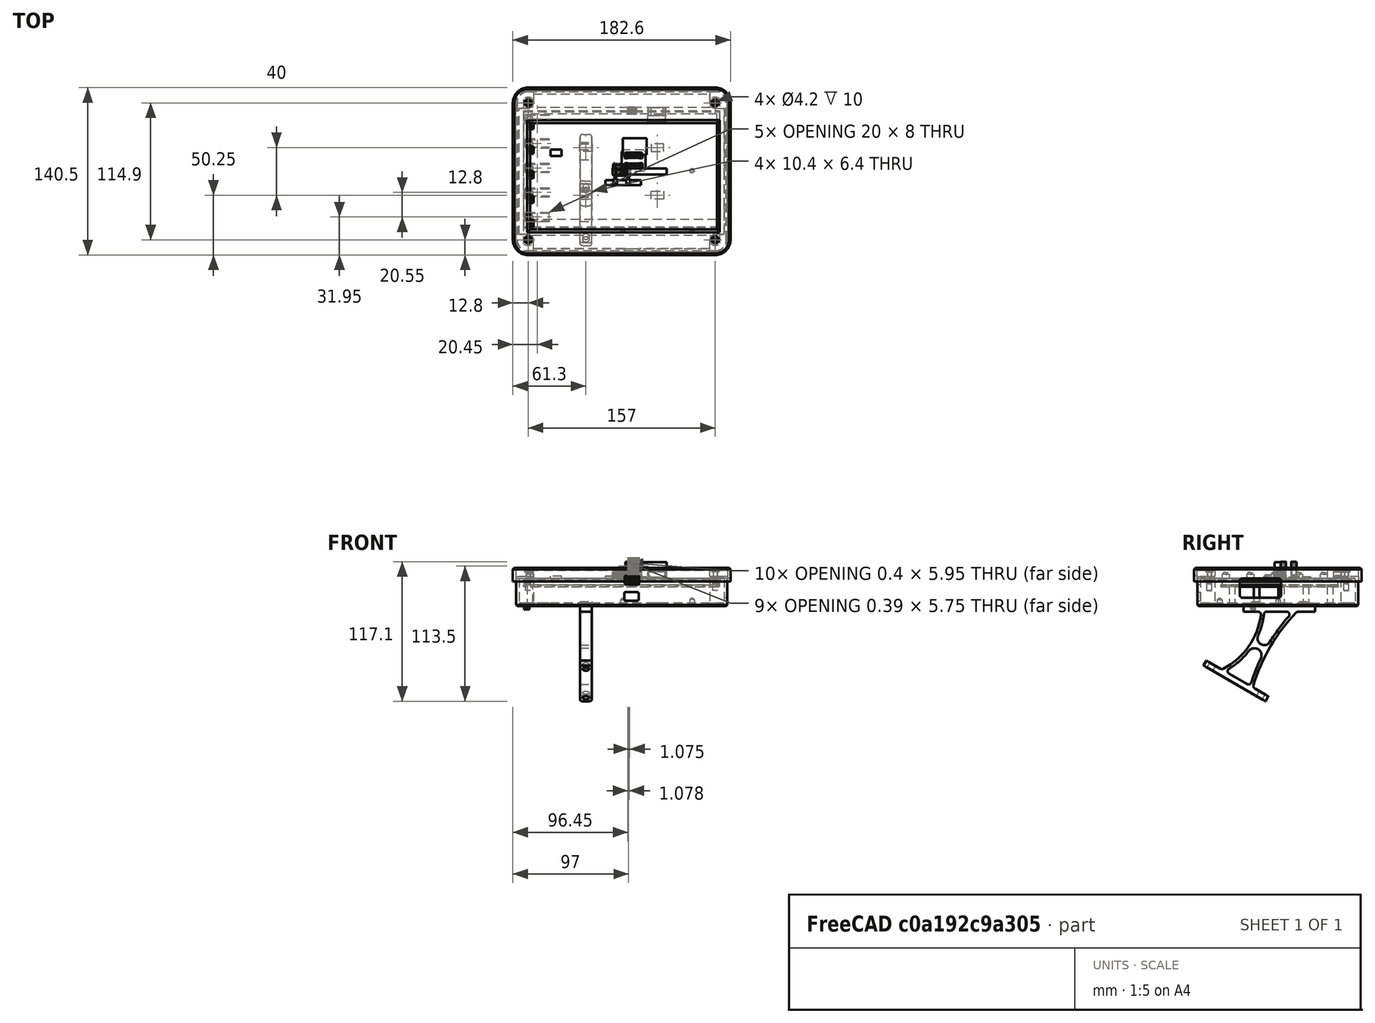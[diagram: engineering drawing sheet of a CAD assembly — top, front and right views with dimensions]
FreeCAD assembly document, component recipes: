
FREECAD ASSEMBLY — COMPONENT RECIPES ("rpi_screen")

This assembly document has 5 components, labeled P0..P4 below (a component is one placed body or linked part). 3 of them carry a construction recipe — the FreeCAD feature program that regenerates the part from scratch, quoted from this document or its linked companion documents; the rest are supplied as boundary geometry only. No exploded tour is included for this assembly.
COMPONENT P0 — geometry summary ("crystal_dfn4 v1"; no construction recipe available for this part):
  bounding box: 3.2 x 2.5 x 0.7 mm
  tessellated surface: 1,094 triangles
  volume: 3 mm^3 (62% of its bounding box)
  symmetry: 2-fold rotationally symmetric about the z axis; mirror-symmetric across its x mid-plane, y mid-plane
COMPONENT P1 — geometry summary ("Rpi+Screen"; no construction recipe available for this part):
  bounding box: 167.4 x 124.7 x 26.8 mm
  tessellated surface: 165,004 triangles
  volume: 114380 mm^3 (20% of its bounding box)
COMPONENT P2 — recipe-attached ("Ensemble boîtier inf", modeled in this document).
Construction recipe (the document's own serialized feature program — sketch geometry with constraints, then the solid features built on it; lengths are millimeters unless a unit is written):

FEATURE [PartDesign::SubShapeBinder] Binder
  BindMode = 0
  ClaimChildren = false
  Context = -> Part021 [Body.Binder.]
  Fuse = false
  MakeFace = true
  PartialLoad = false
  Relative = true
  Support = -> [Part020[Compound.Face122]]
  _Version = 2
FEATURE [Sketcher::SketchObject] Sketch
  ExternalGeometry = -> [Binder]
  FullyConstrained = true
  MapMode = 5
  Support = -> [XY_Plane]
  expr: Constraints[16] = <<Tableau>>.rayon_ext_boitier_inf
  sketch-geometry (8):
    g0: LineSegment StartX=-78.5 StartY=-67.45 StartZ=0 EndX=78.5 EndY=-67.45 EndZ=0
    g1: LineSegment StartX=88.5 StartY=-57.45 StartZ=0 EndX=88.5 EndY=57.45 EndZ=0
    g2: LineSegment StartX=78.5 StartY=67.45 StartZ=0 EndX=-78.5 EndY=67.45 EndZ=0
    g3: LineSegment StartX=-88.5 StartY=57.45 StartZ=0 EndX=-88.5 EndY=-57.45 EndZ=0
    g4: ArcOfCircle CenterX=78.5 CenterY=57.45 CenterZ=0 NormalX=0 NormalY=0 NormalZ=1 AngleXU=0 Radius=10 StartAngle=0 EndAngle=1.5708
    g5: ArcOfCircle CenterX=78.5 CenterY=-57.45 CenterZ=0 NormalX=0 NormalY=0 NormalZ=1 AngleXU=0 Radius=10 StartAngle=4.71239 EndAngle=6.28319
    g6: ArcOfCircle CenterX=-78.5 CenterY=-57.45 CenterZ=0 NormalX=0 NormalY=0 NormalZ=1 AngleXU=0 Radius=10 StartAngle=3.14159 EndAngle=4.71239
    g7: ArcOfCircle CenterX=-78.5 CenterY=57.45 CenterZ=0 NormalX=0 NormalY=0 NormalZ=1 AngleXU=0 Radius=10 StartAngle=1.5708 EndAngle=3.14159
  constraints (19):
    c: Horizontal(g0)
    c: Horizontal(g2)
    c: Vertical(g1)
    c: Vertical(g3)
    c: Tangent(g1,g4) = -1.5708
    c: Tangent(g2,g4) = -1.5708
    c: Tangent(g0,g5) = -1.5708
    c: Tangent(g1,g5) = -1.5708
    c: Tangent(g0,g6) = -1.5708
    c: Tangent(g3,g6) = -1.5708
    c: Tangent(g2,g7) = -1.5708
    c: Tangent(g3,g7) = -1.5708
    c: Equal(g7,g4)
    c: Coincident(g5,g-6)
    c: Coincident(g-3,g4)
    c: Coincident(g6,g-5)
    c: Radius(g4) = 10
    c: DistanceY(g0,g2) = 134.9
    c: DistanceX(g3,g1) = 177
FEATURE [PartDesign::Pad] Pad  label="Pad initial"
  Direction = (1,1,1)
  Length = 23
  Length2 = 100
  Profile = -> Sketch
  Refine = true
  Reversed = true
  Type = 0
FEATURE [Sketcher::SketchObject] Sketch001
  ExternalGeometry = -> [Binder,Sketch]
  FullyConstrained = true
  MapMode = 5
  Support = -> [XY_Plane]
  expr: Constraints[8] = <<Tableau>>.rayon
  expr: Constraints[1] = <<Tableau>>.B4
  sketch-geometry (20):
    g0: LineSegment StartX=-74 StartY=65.05 StartZ=0 EndX=74 EndY=65.05 EndZ=0
    g1: ArcOfCircle CenterX=78.5 CenterY=57.45 CenterZ=0 NormalX=0 NormalY=0 NormalZ=1 AngleXU=0 Radius=4.5 StartAngle=3.14159 EndAngle=4.71239
    g2: LineSegment StartX=86.1 StartY=52.95 StartZ=0 EndX=86.1 EndY=-52.95 EndZ=0
    g3: ArcOfCircle CenterX=78.5 CenterY=-57.45 CenterZ=0 NormalX=0 NormalY=0 NormalZ=1 AngleXU=0 Radius=4.5 StartAngle=1.5708 EndAngle=3.14159
    g4: LineSegment StartX=74 StartY=-65.05 StartZ=0 EndX=-74 EndY=-65.05 EndZ=0
    g5: ArcOfCircle CenterX=-78.5 CenterY=-57.45 CenterZ=0 NormalX=0 NormalY=0 NormalZ=1 AngleXU=0 Radius=4.5 StartAngle=6e-16 EndAngle=1.5708
    g6: LineSegment StartX=-86.1 StartY=-52.95 StartZ=0 EndX=-86.1 EndY=52.95 EndZ=0
    g7: ArcOfCircle CenterX=-78.5 CenterY=57.45 CenterZ=0 NormalX=0 NormalY=0 NormalZ=1 AngleXU=0 Radius=4.5 StartAngle=4.71239 EndAngle=6.28319
    g8: LineSegment StartX=74 StartY=65.05 StartZ=0 EndX=74 EndY=67.45 EndZ=0
    g9: LineSegment StartX=78.5 StartY=52.95 StartZ=0 EndX=86.1 EndY=52.95 EndZ=0
    g10: LineSegment StartX=74 StartY=57.45 StartZ=0 EndX=74 EndY=65.05 EndZ=0
    g11: LineSegment StartX=86.1 StartY=52.95 StartZ=0 EndX=88.5 EndY=52.95 EndZ=0
    g12: LineSegment StartX=86.1 StartY=-52.95 StartZ=0 EndX=78.5 EndY=-52.95 EndZ=0
    g13: LineSegment StartX=74 StartY=-65.05 StartZ=0 EndX=74 EndY=-57.45 EndZ=0
    g14: LineSegment StartX=74 StartY=-65.05 StartZ=0 EndX=74 EndY=-67.45 EndZ=0
    g15: LineSegment StartX=-74 StartY=-65.05 StartZ=0 EndX=-74 EndY=-57.45 EndZ=0
    g16: LineSegment StartX=-86.1 StartY=-52.95 StartZ=0 EndX=-78.5 EndY=-52.95 EndZ=0
    g17: LineSegment StartX=-86.1 StartY=52.95 StartZ=0 EndX=-78.5 EndY=52.95 EndZ=0
    g18: LineSegment StartX=-74 StartY=65.05 StartZ=0 EndX=-74 EndY=57.45 EndZ=0
    g19: LineSegment StartX=-88.5 StartY=52.95 StartZ=0 EndX=-86.1 EndY=52.95 EndZ=0
  constraints (52):
    c: Horizontal(g0)
    c: Distance(g0,g-7) = 2.4
    c: Coincident(g8,g0)
    c: PointOnObject(g8,g-7)
    c: Vertical(g8)
    c: Vertical(g6)
    c: Horizontal(g4)
    c: Vertical(g2)
    c: Radius(g1) = 4.5
    c: Equal(g7,g5)
    c: Equal(g5,g3)
    c: Equal(g3,g1)
    c: Coincident(g9,g2)
    c: Horizontal(g9)
    c: Coincident(g10,g0)
    c: Vertical(g10)
    c: Tangent(g1,g10) = 1.5708
    c: Tangent(g1,g9) = -1.5708
    c: Coincident(g1,g-6)
    c: Coincident(g11,g2)
    c: PointOnObject(g11,g-8)
    c: Horizontal(g11)
    c: Equal(g11,g8)
    c: Coincident(g12,g2)
    c: Horizontal(g12)
    c: Coincident(g13,g4)
    c: Vertical(g13)
    c: Tangent(g3,g13) = 1.5708
    c: Tangent(g3,g12) = -1.5708
    c: Coincident(g3,g-5)
    c: Coincident(g14,g4)
    c: PointOnObject(g14,g-10)
    c: Vertical(g14)
    c: Equal(g14,g11)
    c: Coincident(g15,g4)
    c: Vertical(g15)
    c: Coincident(g16,g6)
    c: Horizontal(g16)
    c: Tangent(g5,g16) = 1.5708
    c: Tangent(g5,g15) = -1.5708
    c: Coincident(g17,g6)
    c: Horizontal(g17)
    c: Tangent(g7,g17) = -1.5708
    c: Coincident(g18,g0)
    c: Vertical(g18)
    c: Tangent(g7,g18) = 1.5708
    c: Coincident(g19,g6)
    c: Horizontal(g19)
    c: PointOnObject(g19,g-9)
    c: Equal(g19,g8)
    c: Coincident(g7,g-3)
    c: Coincident(g5,g-4)
FEATURE [PartDesign::Pocket] Pocket  label="Evidement"
  BaseFeature = -> Pad
  Length = 0
  Length2 = 100
  Offset = -2.4
  Profile = -> Sketch001
  Refine = true
  Type = 3
  UpToFace = -> Pad [Face10]
  expr: Offset = -<<Tableau>>.B4
FEATURE [Sketcher::SketchObject] Sketch002
  ExternalGeometry = -> [Binder,Sketch001]
  FullyConstrained = false
  MapMode = 5
  Support = -> [XY_Plane]
  sketch-geometry (5):
    g0: Circle CenterX=78.5 CenterY=57.45 CenterZ=0 NormalX=0 NormalY=0 NormalZ=1 AngleXU=0 Radius=2.1
    g1: LineSegment StartX=76.6602 StartY=56.4374 StartZ=0 EndX=74.5577 EndY=55.2802 EndZ=0
    g2: Circle CenterX=78.5 CenterY=-57.45 CenterZ=0 NormalX=0 NormalY=0 NormalZ=1 AngleXU=0 Radius=2.1
    g3: Circle CenterX=-78.5 CenterY=-57.45 CenterZ=0 NormalX=0 NormalY=0 NormalZ=1 AngleXU=0 Radius=2.1
    g4: Circle CenterX=-78.5 CenterY=57.45 CenterZ=0 NormalX=0 NormalY=0 NormalZ=1 AngleXU=0 Radius=2.1
  constraints (13):
    c: Radius(g-3) = 1.6
    c: Coincident(g0,g-3)
    c: PointOnObject(g1,g0)
    c: PointOnObject(g1,g-7)
    c: Distance(g1) = 2.4
    c: PointOnObject(g0,g1)
    c: Coincident(g2,g-4)
    c: Coincident(g3,g-5)
    c: Coincident(g4,g-6)
    c: Equal(g4,g3)
    c: Equal(g3,g2)
    c: Equal(g2,g0)
    c: Radius(g0) = 2.1
FEATURE [PartDesign::Pocket] Pocket001  label="Insert"
  BaseFeature = -> Pocket
  Length = 10
  Length2 = 100
  Profile = -> Sketch002
  Refine = true
  Type = 0
FEATURE [PartDesign::SubShapeBinder] Binder001
  BindMode = 0
  ClaimChildren = false
  Context = -> Part021 [Body.Binder001.]
  Fuse = false
  MakeFace = true
  PartialLoad = false
  Relative = true
  Support = -> [Part020[Part018.Compound075.Face74]]
  _Version = 2
FEATURE [Sketcher::SketchObject] Sketch003
  AttachmentOffset = pos=(0,0,-20.6) rot=(0,0,1;0rad)
  ExternalGeometry = -> [Binder001]
  FullyConstrained = true
  MapMode = 5
  Placement = pos=(0,0,-20.6) rot=(0,0,1;0rad)
  Support = -> [XY_Plane]
  expr: .AttachmentOffset.Base.z = -Pad.Length + <<Tableau>>.B4
  sketch-geometry (4):
    g0: Circle CenterX=1.15 CenterY=-48.9 CenterZ=0 NormalX=0 NormalY=0 NormalZ=1 AngleXU=0 Radius=2
    g1: Circle CenterX=59.15 CenterY=-48.9 CenterZ=0 NormalX=0 NormalY=0 NormalZ=1 AngleXU=0 Radius=2
    g2: Circle CenterX=59.15 CenterY=0.1 CenterZ=0 NormalX=0 NormalY=0 NormalZ=1 AngleXU=0 Radius=2
    g3: Circle CenterX=1.15 CenterY=0.1 CenterZ=0 NormalX=0 NormalY=0 NormalZ=1 AngleXU=0 Radius=2
  constraints (8):
    c: Coincident(g0,g-4)
    c: Coincident(g1,g-5)
    c: Coincident(g2,g-6)
    c: Coincident(g3,g-3)
    c: Equal(g3,g2)
    c: Equal(g2,g1)
    c: Equal(g1,g0)
    c: Radius(g3) = 2
FEATURE [PartDesign::Pad] Pad001
  BaseFeature = -> Pocket001
  Direction = (1,1,1)
  Length = 10
  Length2 = 100
  Profile = -> Sketch003
  Refine = true
  Type = 3
  UpToFace = -> Binder001 [Face1]
FEATURE [Sketcher::SketchObject] Sketch004
  ExternalGeometry = -> [Binder001]
  FullyConstrained = true
  MapMode = 5
  Placement = pos=(0,-4.3e-15,-17.75) rot=(1,0,0;3.14159rad)
  Support = -> [Binder001]
  sketch-geometry (4):
    g0: Circle CenterX=1.15 CenterY=-0.1 CenterZ=0 NormalX=0 NormalY=0 NormalZ=1 AngleXU=0 Radius=1.2
    g1: Circle CenterX=59.15 CenterY=-0.1 CenterZ=0 NormalX=0 NormalY=0 NormalZ=1 AngleXU=0 Radius=1.2
    g2: Circle CenterX=59.15 CenterY=48.9 CenterZ=0 NormalX=0 NormalY=0 NormalZ=1 AngleXU=0 Radius=1.2
    g3: Circle CenterX=1.15 CenterY=48.9 CenterZ=0 NormalX=0 NormalY=0 NormalZ=1 AngleXU=0 Radius=1.2
  constraints (8):
    c: Coincident(g0,g-3)
    c: Coincident(g1,g-5)
    c: Coincident(g2,g-6)
    c: Coincident(g3,g-4)
    c: Equal(g3,g0)
    c: Equal(g0,g1)
    c: Equal(g1,g2)
    c: Radius(g0) = 1.2
FEATURE [PartDesign::Pad] Pad002
  BaseFeature = -> Pad001
  Direction = (1,1,1)
  Length = 1
  Length2 = 100
  Profile = -> Sketch004
  Refine = true
  Reversed = true
  Type = 0
FEATURE [PartDesign::Plane] DatumPlane
  AttachmentOffset = pos=(0,0,89) rot=(0,0,1;0rad)
  Length = 151.326
  MapMode = 5
  Placement = pos=(89,-1.98e-14,1.98e-14) rot=(0.57735,0.57735,0.57735;2.0944rad)
  ResizeMode = 0
  Support = -> [YZ_Plane]
  Width = 66.4256
FEATURE [PartDesign::SubShapeBinder] Binder008
  BindMode = 0
  ClaimChildren = false
  Context = -> Part021 [Body.Binder008.]
  Fuse = false
  MakeFace = true
  PartialLoad = false
  Relative = true
  Support = -> [Part020[Compound.Edge128,Compound.Edge136]]
  _Version = 2
FEATURE [PartDesign::SubShapeBinder] Binder009
  BindMode = 0
  ClaimChildren = false
  Context = -> Part021 [Body.Binder009.]
  Fuse = false
  MakeFace = true
  PartialLoad = false
  Relative = true
  Support = -> [Part020[Compound.Edge365,Compound.Edge925]]
  _Version = 2
FEATURE [PartDesign::SubShapeBinder] Binder010
  BindMode = 0
  ClaimChildren = false
  Context = -> Part021 [Body.Binder010.]
  Fuse = false
  MakeFace = true
  PartialLoad = false
  Relative = true
  Support = -> [Part020[Part018.Compound076.Edge439]]
  _Version = 2
FEATURE [Sketcher::SketchObject] Sketch006
  AttachmentOffset = pos=(0,0,69) rot=(0,0,1;0rad)
  ExternalGeometry = -> [Binder008,Binder009,Binder010]
  FullyConstrained = true
  MapMode = 5
  Placement = pos=(0,-69,-1.53e-14) rot=(1,0,0;1.5708rad)
  Support = -> [XZ_Plane]
  expr: Constraints[15] = <<Tableau>>.B2 * 30
  sketch-geometry (13):
    g0: LineSegment StartX=3.87439 StartY=2.425 StartZ=0 EndX=13.4744 EndY=2.425 EndZ=0
    g1: LineSegment StartX=14.6744 StartY=1.225 StartZ=0 EndX=14.6744 EndY=-3.875 EndZ=0
    g2: LineSegment StartX=13.4744 StartY=-5.075 StartZ=0 EndX=3.87439 EndY=-5.075 EndZ=0
    g3: LineSegment StartX=2.67439 StartY=-3.875 StartZ=0 EndX=2.67439 EndY=1.225 EndZ=0
    g4: ArcOfCircle CenterX=3.87439 CenterY=1.225 CenterZ=0 NormalX=0 NormalY=0 NormalZ=1 AngleXU=0 Radius=1.2 StartAngle=1.5708 EndAngle=3.14159
    g5: ArcOfCircle CenterX=13.4744 CenterY=1.225 CenterZ=0 NormalX=0 NormalY=0 NormalZ=1 AngleXU=0 Radius=1.2 StartAngle=0 EndAngle=1.5708
    g6: ArcOfCircle CenterX=13.4744 CenterY=-3.875 CenterZ=0 NormalX=0 NormalY=0 NormalZ=1 AngleXU=0 Radius=1.2 StartAngle=4.71239 EndAngle=6.28319
    g7: ArcOfCircle CenterX=3.87439 CenterY=-3.875 CenterZ=0 NormalX=0 NormalY=0 NormalZ=1 AngleXU=0 Radius=1.2 StartAngle=3.14159 EndAngle=4.71239
    g8: GeomPoint X=8.67439 Y=-1.369 Z=0
    g9: LineSegment StartX=8.67439 StartY=-1.369 StartZ=0 EndX=8.67439 EndY=-1.624 EndZ=0
    g10: LineSegment StartX=11.0744 StartY=-0.15 StartZ=0 EndX=11.0744 EndY=2.425 EndZ=0
    g11: LineSegment StartX=11.7744 StartY=-2.5 StartZ=0 EndX=11.7744 EndY=-5.075 EndZ=0
    g12: LineSegment StartX=8.24488 StartY=-16.15 StartZ=0 EndX=8.67439 EndY=-2.5 EndZ=0
  constraints (33):
    c: Horizontal(g0)
    c: Horizontal(g2)
    c: Vertical(g1)
    c: Vertical(g3)
    c: Tangent(g0,g4) = 1.5708
    c: Tangent(g3,g4) = 1.5708
    c: Tangent(g0,g5) = 1.5708
    c: Tangent(g1,g5) = 1.5708
    c: Tangent(g1,g6) = 1.5708
    c: Tangent(g2,g6) = 1.5708
    c: Tangent(g2,g7) = 1.5708
    c: Tangent(g3,g7) = 1.5708
    c: Equal(g4,g5)
    c: Equal(g5,g6)
    c: Equal(g6,g7)
    c: DistanceX(g3,g1) = 12
    c: Radius(g5) = 1.2
    c: DistanceY(g2,g0) = 7.5
    c: Symmetric(g-3,g-4,g8)
    c: Coincident(g9,g8)
    c: Equal(g9,g-4)
    c: Symmetric(g3,g1,g9)
    c: Coincident(g10,g-6)
    c: PointOnObject(g10,g0)
    c: Vertical(g10)
    c: Coincident(g11,g-5)
    c: PointOnObject(g11,g2)
    c: Vertical(g11)
    c: Equal(g11,g10)
    c: DistanceY(g-7,g-5) = 13.65
    c: Distance(g12) = 13.6568
    c: Symmetric(g-5,g-5,g12)
    c: Coincident(g12,g-7)
FEATURE [PartDesign::SubShapeBinder] Binder011
  BindMode = 0
  ClaimChildren = false
  Context = -> Part021 [Body.Binder011.]
  Fuse = false
  MakeFace = true
  PartialLoad = false
  Relative = true
  Support = -> [Part020[Part018.Compound079.Edge1280,Part018.Compound080.Edge1280,Part018.Compound079.Edge1555,Part018.Compound080.Edge1286]]
  _Version = 2
FEATURE [Sketcher::SketchObject] Sketch005
  ExternalGeometry = -> [Binder011]
  FullyConstrained = true
  MapMode = 5
  Placement = pos=(89,-1.98e-14,1.98e-14) rot=(0.57735,0.57735,0.57735;2.0944rad)
  Support = -> [DatumPlane]
  sketch-geometry (14):
    g0: LineSegment StartX=-29.5843 StartY=-16.175 StartZ=0 EndX=0.415691 EndY=-16.175 EndZ=0
    g1: LineSegment StartX=2.81569 StartY=-13.775 StartZ=0 EndX=2.81569 EndY=-2.175 EndZ=0
    g2: LineSegment StartX=0.415691 StartY=0.225 StartZ=0 EndX=-29.5843 EndY=0.225 EndZ=0
    g3: LineSegment StartX=-31.9843 StartY=-2.175 StartZ=0 EndX=-31.9843 EndY=-13.775 EndZ=0
    g4: ArcOfCircle CenterX=-29.5843 CenterY=-2.175 CenterZ=0 NormalX=0 NormalY=0 NormalZ=1 AngleXU=0 Radius=2.4 StartAngle=1.5708 EndAngle=3.14159
    g5: ArcOfCircle CenterX=0.415691 CenterY=-2.175 CenterZ=0 NormalX=0 NormalY=0 NormalZ=1 AngleXU=0 Radius=2.4 StartAngle=0 EndAngle=1.5708
    g6: ArcOfCircle CenterX=0.415691 CenterY=-13.775 CenterZ=0 NormalX=0 NormalY=0 NormalZ=1 AngleXU=0 Radius=2.4 StartAngle=4.71239 EndAngle=6.28319
    g7: ArcOfCircle CenterX=-29.5843 CenterY=-13.775 CenterZ=0 NormalX=0 NormalY=0 NormalZ=1 AngleXU=0 Radius=2.4 StartAngle=3.14159 EndAngle=4.71239
    g8: GeomPoint X=-14.5843 Y=-7.975 Z=0
    g9: LineSegment StartX=-23.7843 StartY=-0.5 StartZ=0 EndX=-31.9843 EndY=-0.5 EndZ=0
    g10: LineSegment StartX=-29.5843 StartY=0.225 StartZ=0 EndX=-31.9843 EndY=0.225 EndZ=0
    g11: LineSegment StartX=-31.9843 StartY=0.225 StartZ=0 EndX=-31.9843 EndY=-2.175 EndZ=0
    g12: LineSegment StartX=0.415691 StartY=0.225 StartZ=0 EndX=2.81569 EndY=0.225 EndZ=0
    g13: LineSegment StartX=2.81569 StartY=0.225 StartZ=0 EndX=2.81569 EndY=-2.175 EndZ=0
  constraints (34):
    c: Horizontal(g0)
    c: Horizontal(g2)
    c: Vertical(g1)
    c: Vertical(g3)
    c: Tangent(g2,g4) = -1.5708
    c: Tangent(g3,g4) = -1.5708
    c: Tangent(g1,g5) = -1.5708
    c: Tangent(g2,g5) = -1.5708
    c: Tangent(g0,g6) = -1.5708
    c: Tangent(g1,g6) = -1.5708
    c: Tangent(g0,g7) = -1.5708
    c: Tangent(g3,g7) = -1.5708
    c: Equal(g4,g5)
    c: Equal(g5,g6)
    c: Equal(g6,g7)
    c: DistanceX(g3,g1) = 34.8
    c: DistanceY(g0,g2) = 16.4
    c: Symmetric(g-3,g-4,g8)
    c: Symmetric(g7,g5,g8)
    c: Horizontal(g9)
    c: DistanceX(g9,g9) = 8.2
    c: PointOnObject(g9,g3)
    c: Symmetric(g-5,g-5,g9)
    c: Radius(g5) = 2.4
    c: Horizontal(g10)
    c: Coincident(g10,g11)
    c: Vertical(g11)
    c: Horizontal(g12)
    c: Coincident(g12,g13)
    c: Vertical(g13)
    c: Coincident(g10,g2)
    c: Coincident(g11,g3)
    c: Coincident(g2,g12)
    c: Coincident(g1,g13)
FEATURE [PartDesign::Pocket] Pocket002  label="USB"
  BaseFeature = -> Pad002
  Length = 3
  Length2 = 100
  Profile = -> Sketch005
  Refine = true
  Type = 0
  UpToFace = -> Pad002 [Face21]
FEATURE [PartDesign::Pocket] Pocket003  label="µUSB"
  BaseFeature = -> Pocket002
  Length = 5
  Length2 = 100
  Profile = -> Sketch006
  Refine = true
  Type = 0
FEATURE [PartDesign::LinearPattern] LinearPattern  label="Repetition µUSB"
  BaseFeature = -> Pocket003
  Direction = -> Sketch006 [Axis3]
  Length = 13.66
  Occurrences = 2
  Originals = -> [Pocket003]
  Refine = true
  Reversed = true
FEATURE [PartDesign::Chamfer] Chamfer
  Angle = 45
  Base = -> LinearPattern [Face5]
  BaseFeature = -> LinearPattern
  ChamferType = 0
  FlipDirection = false
  Refine = true
  Size = 0.8
  Size2 = 1
  SupportTransform = false
FEATURE [PartDesign::SubShapeBinder] Binder012
  BindMode = 0
  ClaimChildren = false
  Context = -> Part021 [Body.Binder012.]
  Fuse = false
  MakeFace = true
  PartialLoad = false
  Relative = true
  Support = -> [Part020[Compound.Face191,Compound.Face192,Compound.Face193,Compound.Face194,Compound.Face195]]
  _Version = 2
FEATURE [PartDesign::Plane] DatumPlane003
  AttachmentOffset = pos=(0,0,-20.6) rot=(0,0,1;0rad)
  Length = 207.905
  MapMode = 5
  Placement = pos=(0,0,-20.6) rot=(0,0,1;0rad)
  ResizeMode = 0
  Support = -> [XY_Plane]
  Width = 165.805
  expr: .AttachmentOffset.Base.z = -Pad.Length + Spreadsheet.B4
FEATURE [Sketcher::SketchObject] Sketch012
  ExternalGeometry = -> [Binder012]
  FullyConstrained = true
  MapMode = 5
  Placement = pos=(0,0,-20.6) rot=(0,0,1;0rad)
  Support = -> [DatumPlane003]
  sketch-geometry (1):
    g0: Circle CenterX=-76.85 CenterY=-38.3 CenterZ=0 NormalX=0 NormalY=0 NormalZ=1 AngleXU=0 Radius=2.4
  constraints (2):
    c: Coincident(g0,g-3)
    c: Radius(g0) = 2.4
FEATURE [PartDesign::Pad] Pad006
  BaseFeature = -> Chamfer
  Direction = (1,1,1)
  Length = 15
  Length2 = 100
  Offset = -0.4
  Profile = -> Sketch012
  Refine = true
  Type = 0
FEATURE [Sketcher::SketchObject] Sketch013
  ExternalGeometry = -> [Binder012]
  FullyConstrained = true
  MapMode = 5
  Placement = pos=(0,0,-20.6) rot=(0,0,1;0rad)
  Support = -> [DatumPlane003]
  sketch-geometry (11):
    g0: LineSegment StartX=-60.85 StartY=-35.5 StartZ=0 EndX=-79.65 EndY=-35.5 EndZ=0
    g1: LineSegment StartX=-79.65 StartY=-35.5 StartZ=0 EndX=-79.65 EndY=-41.1 EndZ=0
    g2: LineSegment StartX=-79.65 StartY=-41.1 StartZ=0 EndX=-60.85 EndY=-41.1 EndZ=0
    g3: LineSegment StartX=-60.85 StartY=-41.1 StartZ=0 EndX=-60.85 EndY=-42.3 EndZ=0
    g4: LineSegment StartX=-60.85 StartY=-42.3 StartZ=0 EndX=-80.85 EndY=-42.3 EndZ=0
    g5: LineSegment StartX=-80.85 StartY=-42.3 StartZ=0 EndX=-80.85 EndY=-34.3 EndZ=0
    g6: LineSegment StartX=-80.85 StartY=-34.3 StartZ=0 EndX=-60.85 EndY=-34.3 EndZ=0
    g7: LineSegment StartX=-60.85 StartY=-34.3 StartZ=0 EndX=-60.85 EndY=-35.5 EndZ=0
    g8: LineSegment StartX=-80.85 StartY=-35.5 StartZ=0 EndX=-79.65 EndY=-35.5 EndZ=0
    g9: LineSegment StartX=-79.65 StartY=-38.3 StartZ=0 EndX=-76.85 EndY=-38.3 EndZ=0
    g10: LineSegment StartX=-76.85 StartY=-38.3 StartZ=0 EndX=-76.85 EndY=-35.5 EndZ=0
  constraints (32):
    c: Horizontal(g0)
    c: Coincident(g0,g1)
    c: Vertical(g1)
    c: Coincident(g1,g2)
    c: Horizontal(g2)
    c: Coincident(g2,g3)
    c: Vertical(g3)
    c: Coincident(g3,g4)
    c: Horizontal(g4)
    c: Coincident(g4,g5)
    c: Vertical(g5)
    c: Coincident(g5,g6)
    c: Horizontal(g6)
    c: Coincident(g6,g7)
    c: Coincident(g7,g0)
    c: Vertical(g7)
    c: PointOnObject(g8,g5)
    c: Coincident(g8,g0)
    c: Horizontal(g8)
    c: Equal(g8,g7)
    c: Equal(g7,g3)
    c: Equal(g4,g6)
    c: Coincident(g9,g-3)
    c: Horizontal(g9)
    c: Coincident(g10,g9)
    c: PointOnObject(g10,g0)
    c: Vertical(g10)
    c: Equal(g10,g9)
    c: Symmetric(g1,g1,g9)
    c: DistanceY(g7,g7) = 1.2
    c: DistanceX(g9,g9) = 2.8
    c: DistanceX(g6,g6) = 20
FEATURE [PartDesign::Pocket] Pocket008
  BaseFeature = -> Pad006
  Length = 5
  Length2 = 100
  Profile = -> Sketch013
  Refine = true
  Type = 1
FEATURE [PartDesign::SubtractiveSphere] Sphere
  Angle1 = -90
  Angle2 = 90
  Angle3 = 360
  AttacherType = Attacher::AttachEngine3D
  AttachmentOffset = pos=(0,0,22) rot=(0,0,1;0rad)
  BaseFeature = -> Pocket008
  MapMode = 11
  Placement = pos=(-76.85,-38.3,-27.1) rot=(0.707107,-0.707107,0;3.14159rad)
  Radius = 4.8
  Refine = true
  Support = -> [Binder012]
FEATURE [PartDesign::Fillet] Fillet001
  Base = -> Sphere [Edge178,Edge174,Edge176,Edge180]
  BaseFeature = -> Sphere
  Placement = pos=(-76.85,-38.3,-27.1) rot=(0.707107,-0.707107,0;3.14159rad)
  Radius = 0.8
  Refine = true
  SupportTransform = false
FEATURE [PartDesign::LinearPattern] LinearPattern001
  BaseFeature = -> Fillet001
  Direction = -> Sketch012 [V_Axis]
  Length = 82.2
  Occurrences = 5
  Originals = -> [Pad006,Pocket008,Sphere,Fillet001]
  Placement = pos=(-76.85,-38.3,-27.1) rot=(0.707107,-0.707107,0;3.14159rad)
  Refine = true
FEATURE [Sketcher::SketchObject] Sketch019
  FullyConstrained = true
  MapMode = 5
  Placement = pos=(0,0,-20.6) rot=(0,0,1;0rad)
  Support = -> [DatumPlane003]
  sketch-geometry (5):
    g0: LineSegment StartX=24.8 StartY=16.8 StartZ=0 EndX=35.2 EndY=16.8 EndZ=0
    g1: LineSegment StartX=35.2 StartY=16.8 StartZ=0 EndX=35.2 EndY=23.2 EndZ=0
    g2: LineSegment StartX=35.2 StartY=23.2 StartZ=0 EndX=24.8 EndY=23.2 EndZ=0
    g3: LineSegment StartX=24.8 StartY=23.2 StartZ=0 EndX=24.8 EndY=16.8 EndZ=0
    g4: GeomPoint X=30 Y=20 Z=0
  constraints (13):
    c: Coincident(g0,g1)
    c: Coincident(g1,g2)
    c: Coincident(g2,g3)
    c: Coincident(g3,g0)
    c: Horizontal(g0)
    c: Horizontal(g2)
    c: Vertical(g1)
    c: Vertical(g3)
    c: DistanceY(g3,g3) = 6.4
    c: DistanceX(g2,g2) = 10.4
    c: DistanceX(g4) = 30
    c: DistanceY(g4) = 20
    c: Symmetric(g0,g1,g4)
FEATURE [PartDesign::Pocket] Pocket011
  BaseFeature = -> LinearPattern001
  Length = 5
  Length2 = 100
  Placement = pos=(-76.85,-38.3,-27.1) rot=(0.707107,-0.707107,0;3.14159rad)
  Profile = -> Sketch019
  Refine = true
  Type = 1
FEATURE [PartDesign::Mirrored] Mirrored002
  MirrorPlane = -> Sketch019 [H_Axis]
  Placement = pos=(-76.85,-38.3,-27.1) rot=(0.707107,-0.707107,0;3.14159rad)
  Refine = true
FEATURE [PartDesign::Mirrored] Mirrored003
  MirrorPlane = -> YZ_Plane
  Placement = pos=(-76.85,-38.3,-27.1) rot=(0.707107,-0.707107,0;3.14159rad)
  Refine = true
FEATURE [PartDesign::MultiTransform] MultiTransform001
  BaseFeature = -> Pocket011
  Originals = -> [Pocket011]
  Placement = pos=(-76.85,-38.3,-27.1) rot=(0.707107,-0.707107,0;3.14159rad)
  Refine = true
  Transformations = -> [Mirrored002,Mirrored003]
FEATURE [PartDesign::Body] Body  label="Boîtier inférieur"
  Group = -> [Binder,Sketch,Pad,Sketch001,Pocket,Sketch002,Pocket001,Binder001,Sketch003,Pad001,Sketch004,Pad002,DatumPlane,Sketch005,Pocket002,Sketch006,Pocket003,LinearPattern,Chamfer,Binder008,Binder009,Binder010,Binder011,Binder012,DatumPlane003,Sketch012,Pad006,Sketch013,Pocket008,Sphere,Fillet001,LinearPattern001,Sketch019,Pocket011,MultiTransform001,Mirrored002,Mirrored003]
  Origin = -> Origin021
  Tip = -> MultiTransform001
COMPONENT P3 — recipe-attached ("Ensemble boîter sup", modeled in this document).
Construction recipe (the document's own serialized feature program — sketch geometry with constraints, then the solid features built on it; lengths are millimeters unless a unit is written):

FEATURE [PartDesign::SubShapeBinder] Binder002
  BindMode = 0
  ClaimChildren = false
  Context = -> Part022 [Body001.Binder002.]
  Fuse = false
  MakeFace = true
  PartialLoad = false
  Relative = true
  Support = -> [Part020[Compound.Face125]]
  _Version = 2
FEATURE [Sketcher::SketchObject] Sketch007
  ExternalGeometry = -> [Binder002]
  FullyConstrained = true
  MapMode = 5
  Support = -> [XY_Plane001]
  expr: Constraints[15] = <<Tableau>>.rayon_ext_boitier_sup
  sketch-geometry (8):
    g0: LineSegment StartX=-78.5 StartY=-70.25 StartZ=0 EndX=78.5 EndY=-70.25 EndZ=0
    g1: LineSegment StartX=91.3 StartY=-57.45 StartZ=0 EndX=91.3 EndY=57.45 EndZ=0
    g2: LineSegment StartX=78.5 StartY=70.25 StartZ=0 EndX=-78.5 EndY=70.25 EndZ=0
    g3: LineSegment StartX=-91.3 StartY=57.45 StartZ=0 EndX=-91.3 EndY=-57.45 EndZ=0
    g4: ArcOfCircle CenterX=78.5 CenterY=57.45 CenterZ=0 NormalX=0 NormalY=0 NormalZ=1 AngleXU=0 Radius=12.8 StartAngle=0 EndAngle=1.5708
    g5: ArcOfCircle CenterX=78.5 CenterY=-57.45 CenterZ=0 NormalX=0 NormalY=0 NormalZ=1 AngleXU=0 Radius=12.8 StartAngle=4.71239 EndAngle=6.28319
    g6: ArcOfCircle CenterX=-78.5 CenterY=-57.45 CenterZ=0 NormalX=0 NormalY=0 NormalZ=1 AngleXU=0 Radius=12.8 StartAngle=3.14159 EndAngle=4.71239
    g7: ArcOfCircle CenterX=-78.5 CenterY=57.45 CenterZ=0 NormalX=0 NormalY=0 NormalZ=1 AngleXU=0 Radius=12.8 StartAngle=1.5708 EndAngle=3.14159
  constraints (16):
    c: Horizontal(g0)
    c: Horizontal(g2)
    c: Vertical(g1)
    c: Tangent(g1,g4) = -1.5708
    c: Tangent(g2,g4) = -1.5708
    c: Tangent(g0,g5) = -1.5708
    c: Tangent(g1,g5) = -1.5708
    c: Tangent(g0,g6) = -1.5708
    c: Tangent(g3,g6) = -1.5708
    c: Tangent(g2,g7) = -1.5708
    c: Tangent(g3,g7) = -1.5708
    c: Coincident(g-6,g7)
    c: Coincident(g-5,g6)
    c: Coincident(g5,g-4)
    c: Coincident(g-3,g4)
    c: Radius(g4) = 12.8
FEATURE [PartDesign::Pad] Pad003  label="Pad init"
  Direction = (1,1,1)
  Length = 9
  Length2 = 100
  Profile = -> Sketch007
  Refine = true
  Type = 0
FEATURE [Sketcher::SketchObject] Sketch008
  ExternalGeometry = -> [Binder002]
  FullyConstrained = true
  MapMode = 5
  Placement = pos=(0,0,0) rot=(0,1,0;3.14159rad)
  Support = -> [XY_Plane001]
  expr: Constraints[15] = <<Tableau>>.C7 - <<Tableau>>.B4
  sketch-geometry (8):
    g0: LineSegment StartX=-78.5 StartY=-67.85 StartZ=0 EndX=78.5 EndY=-67.85 EndZ=0
    g1: LineSegment StartX=88.9 StartY=-57.45 StartZ=0 EndX=88.9 EndY=57.45 EndZ=0
    g2: LineSegment StartX=78.5 StartY=67.85 StartZ=0 EndX=-78.5 EndY=67.85 EndZ=0
    g3: LineSegment StartX=-88.9 StartY=57.45 StartZ=0 EndX=-88.9 EndY=-57.45 EndZ=0
    g4: ArcOfCircle CenterX=78.5 CenterY=57.45 CenterZ=0 NormalX=0 NormalY=0 NormalZ=1 AngleXU=0 Radius=10.4 StartAngle=0 EndAngle=1.5708
    g5: ArcOfCircle CenterX=78.5 CenterY=-57.45 CenterZ=0 NormalX=0 NormalY=0 NormalZ=1 AngleXU=0 Radius=10.4 StartAngle=4.71239 EndAngle=6.28319
    g6: ArcOfCircle CenterX=-78.5 CenterY=-57.45 CenterZ=0 NormalX=0 NormalY=0 NormalZ=1 AngleXU=0 Radius=10.4 StartAngle=3.14159 EndAngle=4.71239
    g7: ArcOfCircle CenterX=-78.5 CenterY=57.45 CenterZ=0 NormalX=0 NormalY=0 NormalZ=1 AngleXU=0 Radius=10.4 StartAngle=1.5708 EndAngle=3.14159
  constraints (16):
    c: Horizontal(g0)
    c: Horizontal(g2)
    c: Vertical(g1)
    c: Tangent(g1,g4) = -1.5708
    c: Tangent(g2,g4) = -1.5708
    c: Tangent(g0,g5) = -1.5708
    c: Tangent(g1,g5) = -1.5708
    c: Tangent(g0,g6) = -1.5708
    c: Tangent(g3,g6) = -1.5708
    c: Tangent(g2,g7) = -1.5708
    c: Tangent(g3,g7) = -1.5708
    c: Coincident(g-6,g7)
    c: Coincident(g-3,g4)
    c: Coincident(g-4,g5)
    c: Coincident(g6,g-5)
    c: Radius(g4) = 10.4
FEATURE [PartDesign::Pocket] Pocket004  label="Evidement"
  BaseFeature = -> Pad003
  Length = 7
  Length2 = 100
  Profile = -> Sketch008
  Refine = true
  Type = 0
FEATURE [PartDesign::SubShapeBinder] Binder003
  BindMode = 0
  ClaimChildren = false
  Context = -> Part022 [Body001.Binder003.]
  Fuse = false
  MakeFace = true
  PartialLoad = false
  Relative = true
  Support = -> [Part020[Compound.Face14]]
  _Version = 2
FEATURE [Sketcher::SketchObject] Sketch009
  ExternalGeometry = -> [Binder003]
  FullyConstrained = true
  MapMode = 5
  Support = -> [XY_Plane001]
  sketch-geometry (8):
    g0: LineSegment StartX=-76.9 StartY=-48.75 StartZ=0 EndX=79.9 EndY=-48.75 EndZ=0
    g1: LineSegment StartX=79.9 StartY=-48.75 StartZ=0 EndX=79.9 EndY=40.65 EndZ=0
    g2: LineSegment StartX=79.9 StartY=40.65 StartZ=0 EndX=-76.9 EndY=40.65 EndZ=0
    g3: LineSegment StartX=-76.9 StartY=40.65 StartZ=0 EndX=-76.9 EndY=-48.75 EndZ=0
    g4: LineSegment StartX=79.65 StartY=40.4 StartZ=0 EndX=79.9 EndY=40.4 EndZ=0
    g5: LineSegment StartX=79.65 StartY=-48.5 StartZ=0 EndX=79.65 EndY=-48.75 EndZ=0
    g6: LineSegment StartX=-76.9 StartY=-48.5 StartZ=0 EndX=-76.65 EndY=-48.5 EndZ=0
    g7: LineSegment StartX=79.65 StartY=40.4 StartZ=0 EndX=79.65 EndY=40.65 EndZ=0
  constraints (24):
    c: Coincident(g0,g1)
    c: Coincident(g1,g2)
    c: Coincident(g2,g3)
    c: Coincident(g3,g0)
    c: Horizontal(g0)
    c: Horizontal(g2)
    c: Vertical(g1)
    c: Vertical(g3)
    c: Coincident(g4,g-6)
    c: PointOnObject(g4,g1)
    c: Horizontal(g4)
    c: Coincident(g5,g-6)
    c: PointOnObject(g5,g0)
    c: Vertical(g5)
    c: PointOnObject(g6,g3)
    c: Coincident(g6,g-5)
    c: Horizontal(g6)
    c: Coincident(g7,g4)
    c: PointOnObject(g7,g2)
    c: Vertical(g7)
    c: Equal(g4,g5)
    c: Equal(g5,g6)
    c: Equal(g6,g7)
    c: DistanceX(g4,g4) = 0.25
FEATURE [PartDesign::Pocket] Pocket005  label="ouverture écran"
  BaseFeature = -> Pocket004
  Length = 5
  Length2 = 100
  Profile = -> Sketch009
  Refine = true
  Reversed = true
  Type = 1
FEATURE [PartDesign::Plane] DatumPlane001
  AttachmentOffset = pos=(0,0,-7) rot=(0,0,1;0rad)
  Length = 214.635
  MapMode = 5
  Placement = pos=(0,0,7) rot=(0,1,0;3.14159rad)
  ResizeMode = 0
  Support = -> [XY_Plane001]
  Width = 172.535
  expr: .AttachmentOffset.Base.z = -Pocket004.Length
FEATURE [Sketcher::SketchObject] Sketch010
  ExternalGeometry = -> [Binder002]
  FullyConstrained = true
  MapMode = 5
  Placement = pos=(0,0,7) rot=(0,1,0;3.14159rad)
  Support = -> [DatumPlane001]
  expr: Constraints[13] = <<Tableau>>.rayon_ext_boitier_sup - <<Tableau>>.B2
  expr: Constraints[12] = <<Tableau>>.rayon
  sketch-geometry (6):
    g0: LineSegment StartX=74 StartY=-69.85 StartZ=0 EndX=74 EndY=-57.45 EndZ=0
    g1: ArcOfCircle CenterX=78.5 CenterY=-57.45 CenterZ=0 NormalX=0 NormalY=0 NormalZ=1 AngleXU=0 Radius=4.5 StartAngle=1.5708 EndAngle=3.14159
    g2: LineSegment StartX=78.5 StartY=-52.95 StartZ=0 EndX=90.9 EndY=-52.95 EndZ=0
    g3: LineSegment StartX=90.9 StartY=-52.95 StartZ=0 EndX=90.9 EndY=-57.45 EndZ=0
    g4: ArcOfCircle CenterX=78.5 CenterY=-57.45 CenterZ=0 NormalX=0 NormalY=0 NormalZ=1 AngleXU=0 Radius=12.4 StartAngle=4.71239 EndAngle=6.28319
    g5: LineSegment StartX=78.5 StartY=-69.85 StartZ=0 EndX=74 EndY=-69.85 EndZ=0
  constraints (14):
    c: Vertical(g0)
    c: Tangent(g0,g1) = 1.5708
    c: Tangent(g1,g2) = 1.5708
    c: Coincident(g2,g3)
    c: Vertical(g3)
    c: Tangent(g3,g4) = 1.5708
    c: Tangent(g4,g5) = 1.5708
    c: Coincident(g5,g0)
    c: Coincident(g1,g-3)
    c: Coincident(g4,g1)
    c: Horizontal(g5)
    c: Horizontal(g2)
    c: Radius(g1) = 4.5
    c: Radius(g4) = 12.4
FEATURE [PartDesign::Pad] Pad004  label="support ecran"
  BaseFeature = -> Pocket005
  Direction = (1,1,1)
  Length = 10
  Length2 = 100
  Profile = -> Sketch010
  Refine = true
  Reversed = true
  Type = 3
  UpToFace = -> Binder002 [Face1]
FEATURE [PartDesign::Mirrored] Mirrored
  MirrorPlane = -> YZ_Plane001
  Refine = true
FEATURE [PartDesign::Mirrored] Mirrored001
  MirrorPlane = -> XZ_Plane001
  Refine = true
FEATURE [PartDesign::MultiTransform] MultiTransform
  BaseFeature = -> Pad004
  Originals = -> [Pad004]
  Refine = true
  Transformations = -> [Mirrored,Mirrored001]
FEATURE [PartDesign::Plane] DatumPlane002
  AttachmentOffset = pos=(0,0,9) rot=(0,0,1;0rad)
  Length = 214.635
  MapMode = 5
  Placement = pos=(0,0,9) rot=(0,0,1;0rad)
  ResizeMode = 0
  Support = -> [XY_Plane001]
  Width = 172.535
  expr: .AttachmentOffset.Base.z = Pad003.Length
FEATURE [Sketcher::SketchObject] Sketch011
  ExternalGeometry = -> [Binder002]
  FullyConstrained = true
  MapMode = 5
  Placement = pos=(0,0,9) rot=(0,0,1;0rad)
  Support = -> [DatumPlane002]
  sketch-geometry (4):
    g0: Circle CenterX=78.5 CenterY=57.45 CenterZ=0 NormalX=0 NormalY=0 NormalZ=1 AngleXU=0 Radius=2.5
    g1: Circle CenterX=-78.5 CenterY=57.45 CenterZ=0 NormalX=0 NormalY=0 NormalZ=1 AngleXU=0 Radius=2.5
    g2: Circle CenterX=-78.5 CenterY=-57.45 CenterZ=0 NormalX=0 NormalY=0 NormalZ=1 AngleXU=0 Radius=2.5
    g3: Circle CenterX=78.5 CenterY=-57.45 CenterZ=0 NormalX=0 NormalY=0 NormalZ=1 AngleXU=0 Radius=2.5
  constraints (8):
    c: Coincident(g1,g-6)
    c: Coincident(g2,g-5)
    c: Coincident(g3,g-4)
    c: Equal(g3,g2)
    c: Equal(g2,g1)
    c: Equal(g1,g0)
    c: Coincident(g0,g-3)
    c: Radius(g0) = 2.5
FEATURE [PartDesign::Hole] Hole
  BaseFeature = -> MultiTransform
  Depth = 25
  DepthType = 0
  Diameter = 3.6
  DrillForDepth = false
  DrillPoint = 1
  DrillPointAngle = 118
  HoleCutCountersinkAngle = 90
  HoleCutCustomValues = false
  HoleCutDepth = 3.4
  HoleCutDiameter = 6.1
  HoleCutType = 1
  ModelActualThread = false
  Profile = -> Sketch011
  Refine = true
  Tapered = false
  TaperedAngle = 90
  ThreadAngle = 0
  ThreadClass = 0
  ThreadCutOffInner = 0
  ThreadCutOffOuter = 0
  ThreadDirection = 0
  ThreadFit = 2
  ThreadPitch = 0
  ThreadSize = 9
  ThreadType = 1
  Threaded = false
FEATURE [PartDesign::SubShapeBinder] Binder004
  BindMode = 0
  ClaimChildren = false
  Context = -> Part022 [Body001.Binder004.]
  Fuse = false
  MakeFace = true
  PartialLoad = false
  Relative = true
  Support = -> [Hole[Face4]]
  _Version = 2
FEATURE [PartDesign::Pad] Pad005
  BaseFeature = -> Hole
  Direction = (1,1,1)
  Length = 2.4
  Length2 = 100
  Profile = -> Binder004
  Refine = true
  Type = 0
  expr: Length = <<Tableau>>.B4
FEATURE [PartDesign::SubShapeBinder] Binder005
  BindMode = 0
  ClaimChildren = false
  Context = -> Part022 [Body001.Binder005.]
  Fuse = false
  MakeFace = true
  PartialLoad = false
  Relative = true
  Support = -> [Body[Pocket002.Sketch005.]]
  _Version = 2
FEATURE [PartDesign::Pocket] Pocket006
  BaseFeature = -> Pad005
  Length = 9.6
  Length2 = 100
  Midplane = true
  Profile = -> Binder005 [Face1]
  Refine = true
  Reversed = true
  Type = 0
  expr: Length = <<Tableau>>.B4 * 4
FEATURE [PartDesign::SubShapeBinder] Binder006
  BindMode = 0
  ClaimChildren = false
  Context = -> Part022 [Body001.Binder006.]
  Fuse = false
  MakeFace = true
  PartialLoad = false
  Relative = true
  Support = -> [Body[Pocket003.Sketch006.]]
  _Version = 2
FEATURE [PartDesign::Pocket] Pocket007
  BaseFeature = -> Pocket006
  Length = 9.6
  Length2 = 100
  Midplane = true
  Profile = -> Binder006
  Refine = true
  Type = 0
  expr: Length = <<Tableau>>.B4 * 4
FEATURE [PartDesign::SubShapeBinder] Binder007
  BindMode = 0
  ClaimChildren = false
  Context = -> Part022 [Body001.Binder007.]
  Fuse = false
  MakeFace = true
  PartialLoad = false
  Relative = true
  Support = -> [Part020[Compound.Face2]]
  _Version = 2
FEATURE [PartDesign::Chamfer] Chamfer001  label="Chanfrein écran"
  Angle = 45
  Base = -> Pocket007 [Edge89,Edge88,Edge91,Edge90]
  BaseFeature = -> Pocket007
  ChamferType = 1
  FlipDirection = false
  Refine = true
  Size = 2.4
  Size2 = 1.2
  SupportTransform = false
  expr: Size2 = <<Tableau>>.B4 / 2
  expr: Size = <<Tableau>>.B4
FEATURE [PartDesign::Chamfer] Chamfer002  label="Chanfrein périphérie"
  Angle = 45
  Base = -> Chamfer001 [Edge8]
  BaseFeature = -> Chamfer001
  ChamferType = 0
  FlipDirection = false
  Refine = true
  Size = 1.2
  Size2 = 1
  SupportTransform = false
  expr: Size = <<Tableau>>.B4 / 2
FEATURE [PartDesign::Fillet] Fillet  label="Congé USB"
  Base = -> Chamfer002 [Edge111,Edge113]
  BaseFeature = -> Chamfer002
  Radius = 2.4
  Refine = true
  SupportTransform = false
  expr: Radius = <<Tableau>>.B4
FEATURE [PartDesign::Body] Body001  label="Boîtier supérieur"
  Group = -> [Binder002,Sketch007,Pad003,Sketch008,Pocket004,Binder003,Sketch009,Pocket005,DatumPlane001,Sketch010,Pad004,MultiTransform,Mirrored,Mirrored001,DatumPlane002,Sketch011,Hole,Binder004,Pad005,Binder005,Pocket006,Binder006,Pocket007,Binder007,Chamfer001,Chamfer002,Fillet]
  Origin = -> Origin022
  Tip = -> Fillet
COMPONENT P4 — recipe-attached ("Supports", modeled in this document).
Construction recipe (the document's own serialized feature program — sketch geometry with constraints, then the solid features built on it; lengths are millimeters unless a unit is written):

FEATURE [Sketcher::SketchObject] Sketch014
  FullyConstrained = true
  MapMode = 5
  Placement = pos=(0,0,0) rot=(0.57735,0.57735,0.57735;2.0944rad)
  Support = -> [YZ_Plane004]
  sketch-geometry (13):
    g0: LineSegment StartX=-25.9808 StartY=60 StartZ=0 EndX=25.9808 EndY=90 EndZ=0
    g1: LineSegment StartX=-30 StartY=0 StartZ=0 EndX=-30 EndY=4.8 EndZ=0
    g2: LineSegment StartX=-30 StartY=4.8 StartZ=0 EndX=-15 EndY=4.8 EndZ=0
    g3: LineSegment StartX=30 StartY=4.8 StartZ=0 EndX=30 EndY=0 EndZ=0
    g4: LineSegment StartX=-30 StartY=0 StartZ=0 EndX=30 EndY=0 EndZ=0
    g5: LineSegment StartX=-25.9808 StartY=60 StartZ=0 EndX=-23.5808 EndY=55.8431 EndZ=0
    g6: LineSegment StartX=-23.5808 StartY=55.8431 StartZ=0 EndX=-10.5904 EndY=63.3431 EndZ=0
    g7: LineSegment StartX=25.9808 StartY=90 StartZ=0 EndX=28.3808 EndY=85.8431 EndZ=0
    g8: LineSegment StartX=28.3808 StartY=85.8431 StartZ=0 EndX=15.3904 EndY=78.3431 EndZ=0
    g9: ArcOfCircle CenterX=-64.9763 CenterY=38.002 CenterZ=0 NormalX=0 NormalY=0 NormalZ=1 AngleXU=0 Radius=60 StartAngle=5.69679 EndAngle=6.71922
    g10: ArcOfCircle CenterX=160.616 CenterY=40.7996 CenterZ=0 NormalX=0 NormalY=0 NormalZ=1 AngleXU=0 Radius=150 StartAngle=2.88861 EndAngle=3.38396
    g11: LineSegment StartX=15 StartY=4.8 StartZ=0 EndX=30 EndY=4.8 EndZ=0
    g12: GeomPoint X=0 Y=75 Z=0
  constraints (37):
    c: Vertical(g1)
    c: Coincident(g1,g2)
    c: Horizontal(g2)
    c: Coincident(g11,g3)
    c: Vertical(g3)
    c: Coincident(g1,g4)
    c: Horizontal(g4)
    c: Coincident(g0,g5)
    c: Coincident(g5,g6)
    c: Coincident(g0,g7)
    c: Coincident(g7,g8)
    c: Coincident(g9,g6)
    c: Coincident(g10,g8)
    c: Parallel(g6,g8)
    c: Parallel(g6,g0)
    c: Coincident(g2,g9)
    c: Coincident(g11,g10)
    c: Tangent(g2,g11)
    c: Perpendicular(g0,g5)
    c: Perpendicular(g7,g0)
    c: PointOnObject(g6,g8)
    c: Equal(g6,g8)
    c: Coincident(g4,g3)
    c: DistanceY(g1,g1) = 4.8  'epaisseur_base'
    c: DistanceX(g4,g4) = 60
    c: Equal(g2,g11)
    c: Equal(g1,g5)
    c: Distance(g0) = 60
    c: Angle(g0) = 0.523599
    c: Symmetric(g4,g4,g-1)
    c: Radius(g9) = 60
    c: Radius(g10) = 150
    c: DistanceX(g2,g2) = 15
    c: Symmetric(g0,g0,g12)
    c: PointOnObject(g12,g-2)
    c: Equal(g6,g2)
    c: DistanceY(g1,g0) = 60
FEATURE [PartDesign::Pad] Pad007
  Direction = (1,1,1)
  Length = 10
  Length2 = 100
  Midplane = true
  Placement = pos=(0,0,0) rot=(0.57735,0.57735,0.57735;2.0944rad)
  Profile = -> Sketch014
  Refine = true
  Type = 0
FEATURE [Sketcher::SketchObject] Sketch016
  ExternalGeometry = -> [Pad007]
  FullyConstrained = true
  MapMode = 5
  Placement = pos=(0,0,0) rot=(0.57735,0.57735,0.57735;2.0944rad)
  Support = -> [YZ_Plane004]
  sketch-geometry (8):
    g0: LineSegment StartX=-7.96507 StartY=4.8 StartZ=0 EndX=9.50645 EndY=4.8 EndZ=0
    g1: ArcOfCircle CenterX=9.50645 CenterY=7.2 CenterZ=0 NormalX=0 NormalY=0 NormalZ=1 AngleXU=0 Radius=2.4 StartAngle=4.71239 EndAngle=6.50198
    g2: ArcOfCircle CenterX=160.616 CenterY=40.7996 CenterZ=0 NormalX=0 NormalY=0 NormalZ=1 AngleXU=0 Radius=152.4 StartAngle=3.21745 EndAngle=3.36039
    g3: ArcOfCircle CenterX=2.73635 CenterY=28.8 CenterZ=0 NormalX=0 NormalY=0 NormalZ=1 AngleXU=0 Radius=5.93504 StartAngle=0.075859 EndAngle=3.00652
    g4: ArcOfCircle CenterX=-64.9763 CenterY=38.002 CenterZ=0 NormalX=0 NormalY=0 NormalZ=1 AngleXU=0 Radius=62.4 StartAngle=5.78784 EndAngle=6.14812
    g5: ArcOfCircle CenterX=-7.96507 CenterY=7.2 CenterZ=0 NormalX=0 NormalY=0 NormalZ=1 AngleXU=0 Radius=2.4 StartAngle=2.64624 EndAngle=4.71239
    g6: LineSegment StartX=-10.0766 StartY=8.34081 StartZ=0 EndX=-12.1881 EndY=9.48163 EndZ=0
    g7: LineSegment StartX=11.8492 StartY=7.72092 StartZ=0 EndX=14.192 EndY=8.24185 EndZ=0
  constraints (21):
    c: Horizontal(g0)
    c: Tangent(g0,g1) = -1.5708
    c: Tangent(g1,g2) = 1.5708
    c: Tangent(g2,g3) = 1.5708
    c: Tangent(g3,g4) = 1.5708
    c: Tangent(g4,g5) = 1.5708
    c: Tangent(g0,g5) = -1.5708
    c: PointOnObject(g-3,g0)
    c: Coincident(g4,g-3)
    c: Coincident(g2,g-4)
    c: Coincident(g6,g4)
    c: PointOnObject(g6,g-3)
    c: PointOnObject(g4,g6)
    c: Coincident(g7,g1)
    c: PointOnObject(g7,g-4)
    c: PointOnObject(g2,g7)
    c: Equal(g6,g7)
    c: Equal(g5,g1)
    c: Radius(g1) = 2.4
    c: Distance(g7) = 2.4
    c: Distance(g3,g0) = 24
FEATURE [Sketcher::SketchObject] Sketch015
  ExternalGeometry = -> [Sketch014,Sketch016]
  FullyConstrained = true
  MapMode = 5
  Placement = pos=(0,0,0) rot=(0.57735,0.57735,0.57735;2.0944rad)
  Support = -> [YZ_Plane004]
  sketch-geometry (9):
    g0: LineSegment StartX=-6.62652 StartY=65.6316 StartZ=0 EndX=7.76452 EndY=73.9403 EndZ=0
    g1: ArcOfCircle CenterX=8.96452 CenterY=71.8618 CenterZ=0 NormalX=0 NormalY=0 NormalZ=1 AngleXU=0 Radius=2.4 StartAngle=6.08115 EndAngle=8.37758
    g2: ArcOfCircle CenterX=160.616 CenterY=40.7996 CenterZ=0 NormalX=0 NormalY=0 NormalZ=1 AngleXU=0 Radius=152.4 StartAngle=2.93956 EndAngle=3.11406
    g3: ArcOfCircle CenterX=2.66152 CenterY=45.1493 CenterZ=0 NormalX=0 NormalY=0 NormalZ=1 AngleXU=0 Radius=5.61439 StartAngle=3.24687 EndAngle=6.25565
    g4: ArcOfCircle CenterX=-64.9763 CenterY=38.002 CenterZ=0 NormalX=0 NormalY=0 NormalZ=1 AngleXU=0 Radius=62.4 StartAngle=0.10528 EndAngle=0.405315
    g5: ArcOfCircle CenterX=-5.42652 CenterY=63.5532 CenterZ=0 NormalX=0 NormalY=0 NormalZ=1 AngleXU=0 Radius=2.4 StartAngle=2.0944 EndAngle=3.54691
    g6: LineSegment StartX=-7.63206 StartY=62.6068 StartZ=0 EndX=-9.83761 EndY=61.6605 EndZ=0
    g7: LineSegment StartX=11.3157 StartY=71.3802 StartZ=0 EndX=13.6669 EndY=70.8987 EndZ=0
    g8: LineSegment StartX=2.70918 StartY=34.735 StartZ=0 EndX=2.68721 EndY=39.5349 EndZ=0
  constraints (25):
    c: Tangent(g0,g1) = 1.5708
    c: Tangent(g1,g2) = 1.5708
    c: Tangent(g2,g3) = 1.5708
    c: Tangent(g3,g4) = 1.5708
    c: Tangent(g4,g5) = 1.5708
    c: Tangent(g0,g5) = 1.5708
    c: Coincident(g4,g-3)
    c: Coincident(g2,g-4)
    c: Equal(g1,g5)
    c: PointOnObject(g-3,g0)
    c: PointOnObject(g-4,g0)
    c: Coincident(g6,g4)
    c: PointOnObject(g6,g-3)
    c: PointOnObject(g4,g6)
    c: Coincident(g7,g1)
    c: PointOnObject(g7,g-4)
    c: PointOnObject(g2,g7)
    c: Equal(g6,g7)
    c: Radius(g5) = 2.4
    c: Distance(g6) = 2.4
    c: PointOnObject(g8,g-5)
    c: PointOnObject(g8,g3)
    c: PointOnObject(g3,g8)
    c: PointOnObject(g-5,g8)
    c: Distance(g8) = 4.8
FEATURE [Sketcher::SketchObject] Sketch018
  ExternalGeometry = -> [Sketch014]
  FullyConstrained = true
  MapMode = 5
  Placement = pos=(0,0,0) rot=(0.57735,0.57735,0.57735;2.0944rad)
  Support = -> [YZ_Plane004]
  sketch-geometry (7):
    g0: LineSegment StartX=12.9956 StartY=86.8909 StartZ=0 EndX=18.1918 EndY=89.8909 EndZ=0
    g1: LineSegment StartX=18.1918 StartY=89.8909 StartZ=0 EndX=18.7918 EndY=88.8517 EndZ=0
    g2: LineSegment StartX=18.7918 StartY=88.8517 StartZ=0 EndX=17.7526 EndY=88.2517 EndZ=0
    g3: LineSegment StartX=17.7526 StartY=88.2517 StartZ=0 EndX=19.0526 EndY=86 EndZ=0
    g4: LineSegment StartX=19.0526 StartY=86 StartZ=0 EndX=14.8956 EndY=83.6 EndZ=0
    g5: LineSegment StartX=12.9956 StartY=86.8909 StartZ=0 EndX=14.8956 EndY=83.6 EndZ=0
    g6: LineSegment StartX=12.9956 StartY=86.8909 StartZ=0 EndX=7.79948 EndY=83.8909 EndZ=0
  constraints (21):
    c: Coincident(g0,g1)
    c: Coincident(g1,g2)
    c: Coincident(g2,g3)
    c: Coincident(g3,g4)
    c: Coincident(g5,g0)
    c: Perpendicular(g1,g0)
    c: Perpendicular(g2,g1)
    c: Perpendicular(g3,g2)
    c: Perpendicular(g4,g3)
    c: Distance(g1) = 1.2
    c: Equal(g1,g2)
    c: Coincident(g5,g4)
    c: Perpendicular(g4,g5)
    c: Perpendicular(g3,g-3) = 1.5708
    c: Distance(g3) = 2.6
    c: Distance(g4) = 4.8
    c: Distance(g3,g-3) = 8
    c: Coincident(g6,g0)
    c: Parallel(g6,g0)
    c: Equal(g6,g0)
    c: Distance(g0) = 6
FEATURE [PartDesign::Plane] DatumPlane004
  AttachmentOffset = pos=(0,0,4.8) rot=(0,0,1;0rad)
  Length = 60.9545
  MapMode = 5
  Placement = pos=(0,0,4.8) rot=(0,0,1;0rad)
  ResizeMode = 0
  Support = -> [XY_Plane004]
  Width = 70.9545
FEATURE [Sketcher::SketchObject] Sketch017
  FullyConstrained = true
  MapMode = 5
  Placement = pos=(0,0,4.8) rot=(0,0,1;0rad)
  Support = -> [DatumPlane004]
  sketch-geometry (2):
    g0: Circle CenterX=0 CenterY=24 CenterZ=0 NormalX=0 NormalY=0 NormalZ=1 AngleXU=0 Radius=2.4
    g1: Circle CenterX=0 CenterY=-24 CenterZ=0 NormalX=0 NormalY=0 NormalZ=1 AngleXU=0 Radius=2.4
  constraints (5):
    c: PointOnObject(g0,g-2)
    c: Equal(g1,g0)
    c: Symmetric(g1,g0,g-1)
    c: DistanceY(g1,g-1) = 24
    c: Radius(g0) = 2.4
FEATURE [PartDesign::Hole] Hole002
  BaseFeature = -> Pad007
  Depth = 25
  DepthType = 0
  Diameter = 5.5
  DrillForDepth = false
  DrillPoint = 1
  DrillPointAngle = 118
  HoleCutCountersinkAngle = 90
  HoleCutCustomValues = false
  HoleCutDepth = 0
  HoleCutDiameter = 7
  HoleCutType = 0
  ModelActualThread = false
  Placement = pos=(0,0,0) rot=(0.57735,0.57735,0.57735;2.0944rad)
  Profile = -> Sketch017
  Refine = true
  Tapered = false
  TaperedAngle = 90
  ThreadAngle = 0
  ThreadClass = 0
  ThreadCutOffInner = 0
  ThreadCutOffOuter = 0
  ThreadDirection = 0
  ThreadFit = 0
  ThreadPitch = 0
  ThreadSize = 13
  ThreadType = 1
  Threaded = false
FEATURE [PartDesign::Pocket] Pocket009
  BaseFeature = -> Hole002
  Length = 5
  Length2 = 100
  Midplane = true
  Placement = pos=(0,0,0) rot=(0.57735,0.57735,0.57735;2.0944rad)
  Profile = -> Sketch016
  Refine = true
  Type = 1
FEATURE [PartDesign::Pocket] Pocket010
  BaseFeature = -> Pocket009
  Length = 5
  Length2 = 100
  Midplane = true
  Placement = pos=(0,0,0) rot=(0.57735,0.57735,0.57735;2.0944rad)
  Profile = -> Sketch015
  Refine = true
  Type = 1
FEATURE [PartDesign::Pad] Pad008
  BaseFeature = -> Pocket010
  Direction = (1,1,1)
  Length = 10
  Length2 = 100
  Midplane = true
  Placement = pos=(0,0,0) rot=(0.57735,0.57735,0.57735;2.0944rad)
  Profile = -> Sketch018
  Refine = true
  Type = 0
FEATURE [PartDesign::LinearPattern] LinearPattern002
  BaseFeature = -> Pad008
  Direction = -> Sketch018 [Axis0]
  Length = 40
  Occurrences = 2
  Originals = -> [Pad008]
  Placement = pos=(0,0,0) rot=(0.57735,0.57735,0.57735;2.0944rad)
  Refine = true
FEATURE [PartDesign::Fillet] Fillet002
  Base = -> LinearPattern002 [Edge36,Edge8,Edge39,Edge59,Edge4,Edge3,Edge33,Edge32,Edge55,Edge56,Edge47,Edge48]
  BaseFeature = -> LinearPattern002
  Placement = pos=(0,0,0) rot=(0.57735,0.57735,0.57735;2.0944rad)
  Radius = 2.4
  Refine = true
  SupportTransform = false
FEATURE [PartDesign::Body] Body002  label="Support"
  Group = -> [Sketch014,Pad007,Sketch016,Sketch017,DatumPlane004,Hole002,Pocket009,Sketch015,Pocket010,Sketch018,Pad008,LinearPattern002,Fillet002]
  Origin = -> Origin025
  Placement = pos=(30,-36.4,-88) rot=(-1,0,0;0.523599rad)
  Tip = -> Fillet002
FEATURE [PartDesign::FeatureBase] Clone
  BaseFeature = -> Body002
  Placement = pos=(20,-36.4,-88) rot=(-1,0,0;0.523599rad)
FEATURE [PartDesign::Body] Body003  label="Support2"
  BaseFeature = -> Body002
  Group = -> [Clone]
  Origin = -> Origin026
  Placement = pos=(-50,0,0) rot=(0,0,1;0rad)
  Tip = -> Clone
PROVENANCE & LICENSES
A FreeCAD (.FCStd) document from a public repository crawl; recipes are the document's own serialized feature recipes (and, for linked parts, companion documents' recipes).
License: cc0-1.0.
